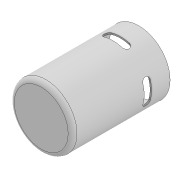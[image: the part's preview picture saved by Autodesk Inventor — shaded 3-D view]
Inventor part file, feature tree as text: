
AUTODESK INVENTOR PART (.ipt)
format: ipt  version: 2020 (Build 240168000, 168)  size: 198,656 bytes
history: native  units: mm
features: extrude x5, sketch x5, other x2, fillet x1, shell x1, pattern_circular x1
ambient origin geometry x8: Origin, YZ Plane, XZ Plane, XY Plane, X Axis, Y Axis, Z Axis, Center Point
bodies: Body1 (feature_tree)
feature tree (15):
  other  "솔리드1"
  extrude  "돌출1"  Depth=42.4mm
  extrude  "돌출2"  Depth=30.0mm TaperAngle=0.0deg
  extrude  "돌출3"  Depth=42.4mm
  fillet  "모깎기1"  Radius=30.0mm
  shell  "쉘1"  Thickness=42.4mm
  other  "작업 평면1"
  extrude  "돌출12"  Depth=6.0mm TaperAngle=0.0deg
  pattern_circular  "원형 패턴2"  [2 undecoded]
  extrude  "돌출13"  Depth=60.0mm
  sketch  "스케치1"
  sketch  "스케치2"
  sketch  "스케치3"
  sketch  "스케치12"
  sketch  "스케치13"
note: 2 required parameter values undecoded (feature->parameter linkage not recoverable at this tier; creation-order binding heuristic only, values carry confidence <= 0.55)
